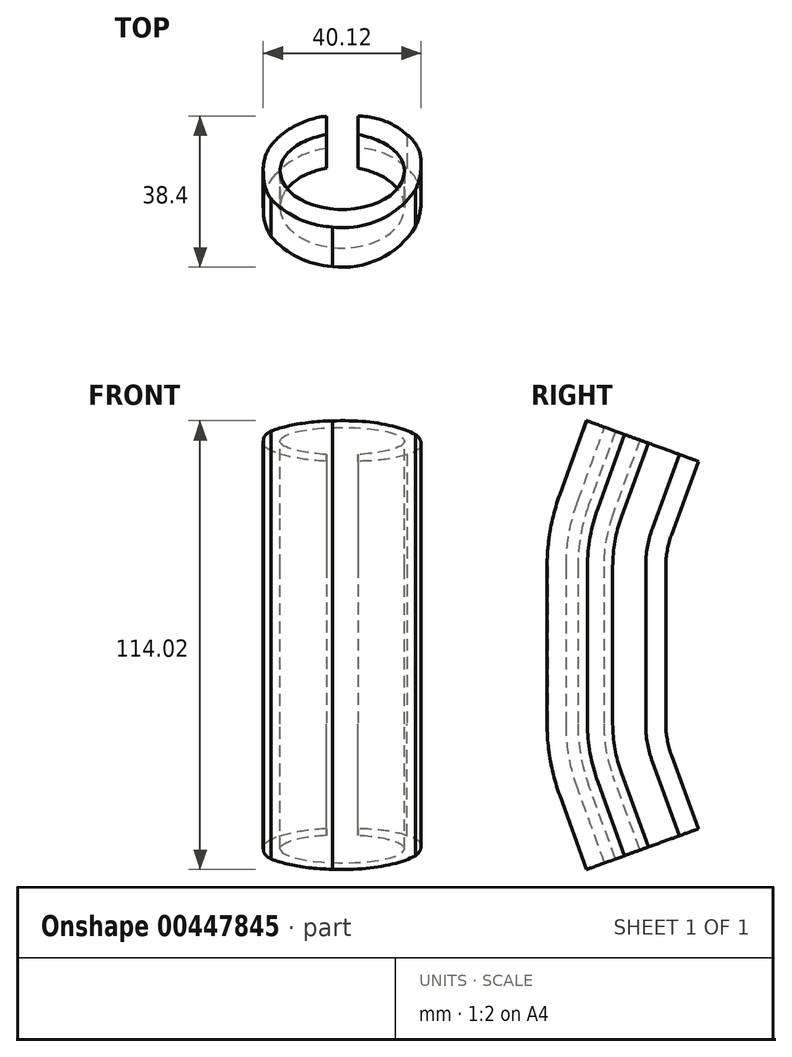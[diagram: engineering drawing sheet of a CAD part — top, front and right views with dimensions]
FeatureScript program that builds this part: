
annotation { "Feature Type Name" : "Feature", "Feature Type Description" : "" }
export const myFeature = defineFeature(function(context is Context, id is Id, definition is map)
    precondition{}
    {
        {
            var Q0;
            Q0=qCreatedBy(makeId("Top.planeOp"),FACE);
            var sketch = newSketch(context, id + "F0", { "sketchPlane" : qUnion([Q0])});
            skLineSegment(sketch, "E0.left", {"start": v(20, 1.5) * mm, "end": v(20, 1.48) * mm});
            skPoint(sketch, "E0.middle", {"position": v(0, 0) * mm});
            skPoint(sketch, "E1", {"position": v(4, 15) * mm});
            skPoint(sketch, "E2", {"position": v(-4, 15) * mm});
            skLineSegment(sketch, "E3", {"start": v(-4, 15) * mm, "end": v(-4, 10) * mm});
            skLineSegment(sketch, "E4", {"start": v(4, 15) * mm, "end": v(4, 10) * mm});
            skEllipticalArc(sketch, "E5", {});
            skLineSegment(sketch, "E6", {"start": v(-4, 10) * mm, "end": v(-4, 9.97) * mm});
            skLineSegment(sketch, "E7", {"start": v(-4, 9.97) * mm, "end": v(-4, 9.97) * mm});
            skLineSegment(sketch, "E8", {"start": v(4, 10) * mm, "end": v(4, 9.97) * mm});
            skArc(sketch, "E9", {"start": v(16.5, 9.9) * mm, "mid": v(10.75, 13.67) * mm, "end": v(4, 15) * mm});
            skArc(sketch, "E10", {"start": v(20, 1.5) * mm, "mid": v(19.3, 6.13) * mm, "end": v(16.5, 9.9) * mm});
            skArc(sketch, "E11", {"start": v(18.62, -4.9) * mm, "mid": v(19.65, -1.77) * mm, "end": v(20, 1.5) * mm});
            skArc(sketch, "E12", {"start": v(-2.53, -15) * mm, "mid": v(9.53, -13.05) * mm, "end": v(18.62, -4.9) * mm});
            skArc(sketch, "E13", {"start": v(-18.1, -7.36) * mm, "mid": v(-11.1, -12.76) * mm, "end": v(-2.53, -15) * mm});
            skArc(sketch, "E14", {"start": v(-20, -0.76) * mm, "mid": v(-19.55, -4.2) * mm, "end": v(-18.1, -7.36) * mm});
            skArc(sketch, "E15", {"start": v(-16.89, 8.53) * mm, "mid": v(-19.49, 4.23) * mm, "end": v(-20, -0.76) * mm});
            skArc(sketch, "E16", {"start": v(-4, 15) * mm, "mid": v(-11, 12.86) * mm, "end": v(-16.89, 8.53) * mm});
            skPoint(sketch, "E17.orphan", {"position": v(-20, 15) * mm});
            skPoint(sketch, "E18.orphan", {"position": v(-20, -15) * mm});
            skPoint(sketch, "E19.orphan", {"position": v(20, -15) * mm});
            skPoint(sketch, "E0.bottom.start.orphan", {"position": v(20, 15) * mm});
            skLineSegment(sketch, "E20", {"start": v(-20.01, 38.1) * mm, "end": v(22.77, 38.1) * mm});
            const initialGuessF0  = {"E5": [0, 0, 1, 0, 0.01581776735740709, 0.010301972391768015, 1.8265548117543458, 1.3149814284072967]};
            skSetInitialGuess(sketch, initialGuessF0);
            skSolve(sketch);
        }
        {
            var Q0;
            Q0=makeQuery(id+"F0.imprint","IMPRINT",FACE,{"disambiguationData":[TD([[makeQuery(id+"F0.imprint","IMPRINT",EDGE,{"derivedFrom":sQuery(id+"F0.wireOp",EDGE,"E3")}),-1.0]])]});
            var Q1;
            Q1=sQuery(id+"F0.wireOp",EDGE,"E20");
            revolve(context, id + "F1", {"entities" : qUnion([Q0]), "axis" : qUnion([Q1]), "revolveType" : RevolveType.ONE_DIRECTION, "angle" : 20 * degree});
        }
        {
            var Q0;
            Q0=makeQuery(id+"F1.opRevolve","CAP_FACE",FACE,{"disambiguationData":[OSD([sQuery(id+"F0.wireOp",EDGE,"E3"),sQuery(id+"F0.wireOp",EDGE,"E4"),sQuery(id+"F0.wireOp",EDGE,"E5"),sQuery(id+"F0.wireOp",EDGE,"E6"),sQuery(id+"F0.wireOp",EDGE,"E8"),sQuery(id+"F0.wireOp",EDGE,"E9"),sQuery(id+"F0.wireOp",EDGE,"E10"),sQuery(id+"F0.wireOp",EDGE,"E11"),sQuery(id+"F0.wireOp",EDGE,"E12"),sQuery(id+"F0.wireOp",EDGE,"E13"),sQuery(id+"F0.wireOp",EDGE,"E14"),sQuery(id+"F0.wireOp",EDGE,"E15"),sQuery(id+"F0.wireOp",EDGE,"E16")])],"isStart":true});
            extrude(context, id + "F2", {"entities" : qUnion([Q0]), "operationType" : NewBodyOperationType.ADD, "depth" : 40 * mm});
        }
        {
            var Q0;
            Q0=makeQuery(id+"F1.opRevolve","CAP_FACE",FACE,{"disambiguationData":[OSD([sQuery(id+"F0.wireOp",EDGE,"E3"),sQuery(id+"F0.wireOp",EDGE,"E4"),sQuery(id+"F0.wireOp",EDGE,"E5"),sQuery(id+"F0.wireOp",EDGE,"E6"),sQuery(id+"F0.wireOp",EDGE,"E8"),sQuery(id+"F0.wireOp",EDGE,"E9"),sQuery(id+"F0.wireOp",EDGE,"E10"),sQuery(id+"F0.wireOp",EDGE,"E11"),sQuery(id+"F0.wireOp",EDGE,"E12"),sQuery(id+"F0.wireOp",EDGE,"E13"),sQuery(id+"F0.wireOp",EDGE,"E14"),sQuery(id+"F0.wireOp",EDGE,"E15"),sQuery(id+"F0.wireOp",EDGE,"E16")])],"isStart":false});
            extrude(context, id + "F3", {"entities" : qUnion([Q0]), "operationType" : NewBodyOperationType.ADD, "depth" : 20 * mm});
        }
        {
            var Q0;
            Q0=qCreatedBy(makeId("Top.planeOp"),FACE);
            cPlane(context, id + "F4", {"entities" : qUnion([Q0]), "cplaneType" : CPlaneType.OFFSET, "offset" : 20 * mm, "width" : 150 * mm, "height" : 150 * mm});
        }
        {
            var Q0;
            Q0=makeQuery(id+"F1.opRevolve","SWEPT_BODY",BODY,{"disambiguationData":[OSD([sQuery(id+"F0.wireOp",EDGE,"E3"),sQuery(id+"F0.wireOp",EDGE,"E4"),sQuery(id+"F0.wireOp",EDGE,"E5"),sQuery(id+"F0.wireOp",EDGE,"E6"),sQuery(id+"F0.wireOp",EDGE,"E8"),sQuery(id+"F0.wireOp",EDGE,"E9"),sQuery(id+"F0.wireOp",EDGE,"E10"),sQuery(id+"F0.wireOp",EDGE,"E11"),sQuery(id+"F0.wireOp",EDGE,"E12"),sQuery(id+"F0.wireOp",EDGE,"E13"),sQuery(id+"F0.wireOp",EDGE,"E14"),sQuery(id+"F0.wireOp",EDGE,"E15"),sQuery(id+"F0.wireOp",EDGE,"E16")])]});
            var Q1;
            Q1=qCreatedBy(id+"F4.planeOp",FACE);
            mirror(context, id + "F5", {"operationType" : NewBodyOperationType.ADD, "entities" : qUnion([Q0]), "mirrorPlane" : qUnion([Q1])});
        }
    });
